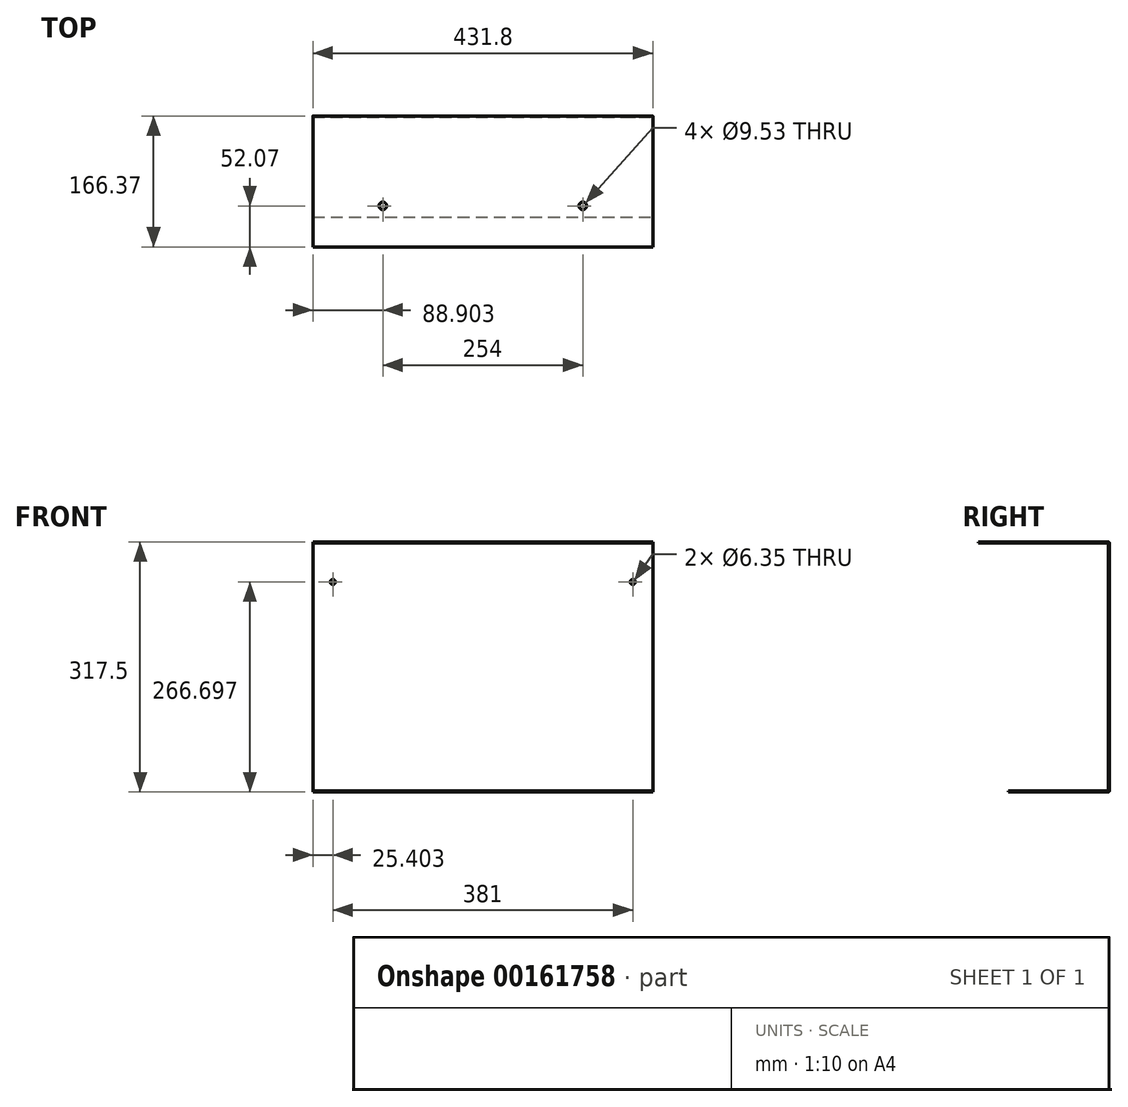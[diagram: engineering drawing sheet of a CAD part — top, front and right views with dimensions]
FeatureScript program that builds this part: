
annotation { "Feature Type Name" : "Feature", "Feature Type Description" : "" }
export const myFeature = defineFeature(function(context is Context, id is Id, definition is map)
    precondition{}
    {
        {
            var Q0;
            Q0=qCreatedBy(makeId("Front.planeOp"),FACE);
            var sketch = newSketch(context, id + "F0", { "sketchPlane" : qUnion([Q0])});
            skLineSegment(sketch, "E0.bottom", {"start": v(-200.93, 163.95) * mm, "end": v(230.87, 163.95) * mm});
            skLineSegment(sketch, "E0.top", {"start": v(-200.93, -153.55) * mm, "end": v(230.87, -153.55) * mm});
            skLineSegment(sketch, "E0.left", {"start": v(-200.93, 163.95) * mm, "end": v(-200.93, -153.55) * mm});
            skLineSegment(sketch, "E0.right", {"start": v(230.87, 163.95) * mm, "end": v(230.87, -153.55) * mm});
            skSolve(sketch);
        }
        {
            var Q0;
            Q0 = qSketchRegion(id + "F0", true);
            extrude(context, id + "F1", {"entities" : qUnion([Q0]), "depth" : 1.27 * mm});
        }
        {
            var Q0;
            Q0=makeQuery(id+"F1.opExtrude","CAP_FACE",FACE,{"disambiguationData":[OSD([sQuery(id+"F0.wireOp",EDGE,"E0.bottom"),sQuery(id+"F0.wireOp",EDGE,"E0.top"),sQuery(id+"F0.wireOp",EDGE,"E0.left"),sQuery(id+"F0.wireOp",EDGE,"E0.right")])],"isStart":false});
            var sketch = newSketch(context, id + "F2", { "sketchPlane" : qUnion([Q0])});
            skLineSegment(sketch, "E1.bottom", {"start": v(-200.93, 163.95) * mm, "end": v(230.87, 163.95) * mm});
            skLineSegment(sketch, "E1.top", {"start": v(-200.93, 162.68) * mm, "end": v(230.87, 162.68) * mm});
            skLineSegment(sketch, "E1.left", {"start": v(-200.93, 163.95) * mm, "end": v(-200.93, 162.68) * mm});
            skLineSegment(sketch, "E1.right", {"start": v(230.87, 163.95) * mm, "end": v(230.87, 162.68) * mm});
            skSolve(sketch);
        }
        {
            var Q0;
            Q0=makeQuery(id+"F2.imprint","IMPRINT",FACE,{"disambiguationData":[TD([[makeQuery(id+"F2.imprint","IMPRINT",EDGE,{"derivedFrom":sQuery(id+"F2.wireOp",EDGE,"E1.bottom")}),-1.0]])]});
            extrude(context, id + "F3", {"entities" : qUnion([Q0]), "operationType" : NewBodyOperationType.ADD, "depth" : 165.1 * mm});
        }
        {
            var Q0;
            Q0=makeQuery(id+"F3.opExtrude","CAP_EDGE",EDGE,{"disambiguationData":[OSD([sQuery(id+"F2.wireOp",EDGE,"E1.top")])],"isStart":true});
            var Q1;
            Q1=makeQuery(id+"F1.opExtrude","CAP_EDGE",EDGE,{"disambiguationData":[OSD([sQuery(id+"F0.wireOp",EDGE,"E0.bottom")])],"isStart":true});
            fillet(context, id + "F4", {"entities" : qUnion([Q0, Q1]), "radius" : 1.27 * mm, "tangentPropagation" : true, "allowEdgeOverflow" : false});
        }
        {
            var Q0;
            Q0=makeQuery(id+"F1.opExtrude","CAP_FACE",FACE,{"disambiguationData":[OSD([sQuery(id+"F0.wireOp",EDGE,"E0.bottom"),sQuery(id+"F0.wireOp",EDGE,"E0.top"),sQuery(id+"F0.wireOp",EDGE,"E0.left"),sQuery(id+"F0.wireOp",EDGE,"E0.right")])],"isStart":false});
            var sketch = newSketch(context, id + "F5", { "sketchPlane" : qUnion([Q0])});
            skLineSegment(sketch, "E2.bottom", {"start": v(-200.93, -153.55) * mm, "end": v(230.87, -153.55) * mm});
            skLineSegment(sketch, "E2.top", {"start": v(-200.93, -152.28) * mm, "end": v(230.87, -152.28) * mm});
            skLineSegment(sketch, "E2.left", {"start": v(-200.93, -153.55) * mm, "end": v(-200.93, -152.28) * mm});
            skLineSegment(sketch, "E2.right", {"start": v(230.87, -153.55) * mm, "end": v(230.87, -152.28) * mm});
            skSolve(sketch);
        }
        {
            var Q0;
            Q0 = qSketchRegion(id + "F5", true);
            extrude(context, id + "F6", {"entities" : qUnion([Q0]), "operationType" : NewBodyOperationType.ADD, "depth" : 127 * mm});
        }
        {
            var Q0;
            Q0=makeQuery(id+"F6.opExtrude","CAP_EDGE",EDGE,{"disambiguationData":[OSD([sQuery(id+"F5.wireOp",EDGE,"E2.top")])],"isStart":true});
            var Q1;
            Q1=makeQuery(id+"F1.opExtrude","CAP_EDGE",EDGE,{"disambiguationData":[OSD([sQuery(id+"F0.wireOp",EDGE,"E0.top")])],"isStart":true});
            fillet(context, id + "F7", {"entities" : qUnion([Q0, Q1]), "radius" : 1.27 * mm, "tangentPropagation" : true, "allowEdgeOverflow" : false});
        }
        {
            var Q0;
            Q0=makeQuery(id+"F1.opExtrude","CAP_FACE",FACE,{"disambiguationData":[OSD([sQuery(id+"F0.wireOp",EDGE,"E0.bottom"),sQuery(id+"F0.wireOp",EDGE,"E0.top"),sQuery(id+"F0.wireOp",EDGE,"E0.left"),sQuery(id+"F0.wireOp",EDGE,"E0.right")])],"isStart":false});
            var sketch = newSketch(context, id + "F8", { "sketchPlane" : qUnion([Q0])});
            skCircle(sketch, "E3", {"center": v(-175.53, 113.15) * mm, "radius": 3.18 * mm});
            skCircle(sketch, "E4", {"center": v(205.47, 113.15) * mm, "radius": 3.18 * mm});
            skSolve(sketch);
        }
        {
            var Q0;
            Q0 = qSketchRegion(id + "F8", true);
            extrude(context, id + "F9", {"entities" : qUnion([Q0]), "operationType" : NewBodyOperationType.REMOVE, "oppositeDirection" : true, "depth" : 25.4 * mm, "offsetDistance" : 25.4 * mm});
        }
        {
            var Q0;
            Q0=makeQuery(id+"F3.boolean.opBoolean","MERGE",FACE,{"derivedFrom":[makeQuery(id+"F1.opExtrude","SWEPT_FACE",FACE,{"disambiguationData":[OSD([sQuery(id+"F0.wireOp",EDGE,"E0.bottom")])]}),makeQuery(id+"F3.opExtrude","SWEPT_FACE",FACE,{"disambiguationData":[OSD([sQuery(id+"F2.wireOp",EDGE,"E1.bottom")])]})]});
            var sketch = newSketch(context, id + "F10", { "sketchPlane" : qUnion([Q0])});
            skCircle(sketch, "E5", {"center": v(-112.03, -114.3) * mm, "radius": 4.76 * mm});
            skCircle(sketch, "E6", {"center": v(141.97, -114.3) * mm, "radius": 4.76 * mm});
            skSolve(sketch);
        }
        {
            var Q0;
            Q0 = qSketchRegion(id + "F10", true);
            extrude(context, id + "F11", {"entities" : qUnion([Q0]), "operationType" : NewBodyOperationType.REMOVE, "endBound" : BoundingType.THROUGH_ALL, "oppositeDirection" : true, "depth" : 25.4 * mm, "offsetDistance" : 25.4 * mm});
        }
    });
